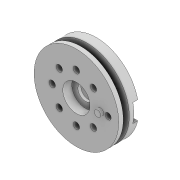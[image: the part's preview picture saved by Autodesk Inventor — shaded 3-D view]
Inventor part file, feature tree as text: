
AUTODESK INVENTOR PART (.ipt)
format: ipt  version: 2022 (Build 260153000, 153)  size: 249,856 bytes
history: native  units: mm
features: extrude x9, sketch x9, projected_geometry x4, revolve x1, pattern_circular x1
ambient origin geometry x8: Origin, YZ Plane, XZ Plane, XY Plane, X Axis, Y Axis, Z Axis, Center Point
bodies: Solid1 (feature_tree)
feature tree (24):
  revolve  "Revolution1"  [1 undecoded]
  extrude  "Extrusion1"  Depth=1.5mm
  pattern_circular  "Circular Pattern1"  Count=10  [1 undecoded]
  extrude  "Extrusion2"  Depth=2.0mm
  extrude  "Extrusion3"  Depth=0.5mm TaperAngle=0.0deg
  extrude  "Extrusion8"  Depth=4.0mm
  extrude  "Extrusion6"  Depth=5.0mm TaperAngle=0.0deg
  extrude  "Extrusion7"  Depth=0.5mm
  sketch  "Sketch11"  dims[d16=10.5mm d17=100.0mm d18=0.0mm d19=4.0mm d20=5.0mm d21=0.0mm d24=10.25mm d25=2.0mm d26=0.0mm d31=2.0mm d32=4.0mm d33=0.0mm d34=18.0mm d35=1.5mm d36=0.0mm d37=5.0mm d38=1.0mm d39=0.0mm d40=100.0mm d41=0.0mm d44=4.0mm d45=4.0mm d46=4.0mm d47=4.0mm d48=4.0mm d49=4.0mm d50=4.0mm d51=3.0mm d52=3.0mm d53=3.0mm d54=1.6mm d55=0.0mm d56=6.0mm d57=0.0mm d42=0.5mm d43=0.872665mm]
  extrude  "Extrusion10"  Depth=2.0mm TaperAngle=0.0deg
  extrude  "Extrusion11"  Depth=2.0mm
  extrude  "Extrusion9"  Depth=4.0mm TaperAngle=0.0deg
  sketch  "Sketch1"  dims[d0=5.0mm d1=3.0mm]
  sketch  "Sketch2"  dims[d2=14.0mm d4=1.5mm]
  sketch  "Sketch3"  dims[d5=1.5mm]
  sketch  "Sketch4"  dims[d6=360.0deg]
  projected_geometry  "Projected Loop1"
  projected_geometry  "Projected Loop2"
  sketch  "Sketch7"  dims[d7=2.1mm]
  sketch  "Sketch8"  dims[d8=8.0mm]
  projected_geometry  "Projected Loop5"
  sketch  "Sketch9"  dims[d9=9.0mm d10=100.0mm d11=0.0mm]
  sketch  "Sketch10"  dims[d12=80.0mm d13=360.0deg d15=2.0mm]
  projected_geometry  "Project Cut Edges1"
note: 2 required parameter values undecoded (feature->parameter linkage not recoverable at this tier; creation-order binding heuristic only, values carry confidence <= 0.55)